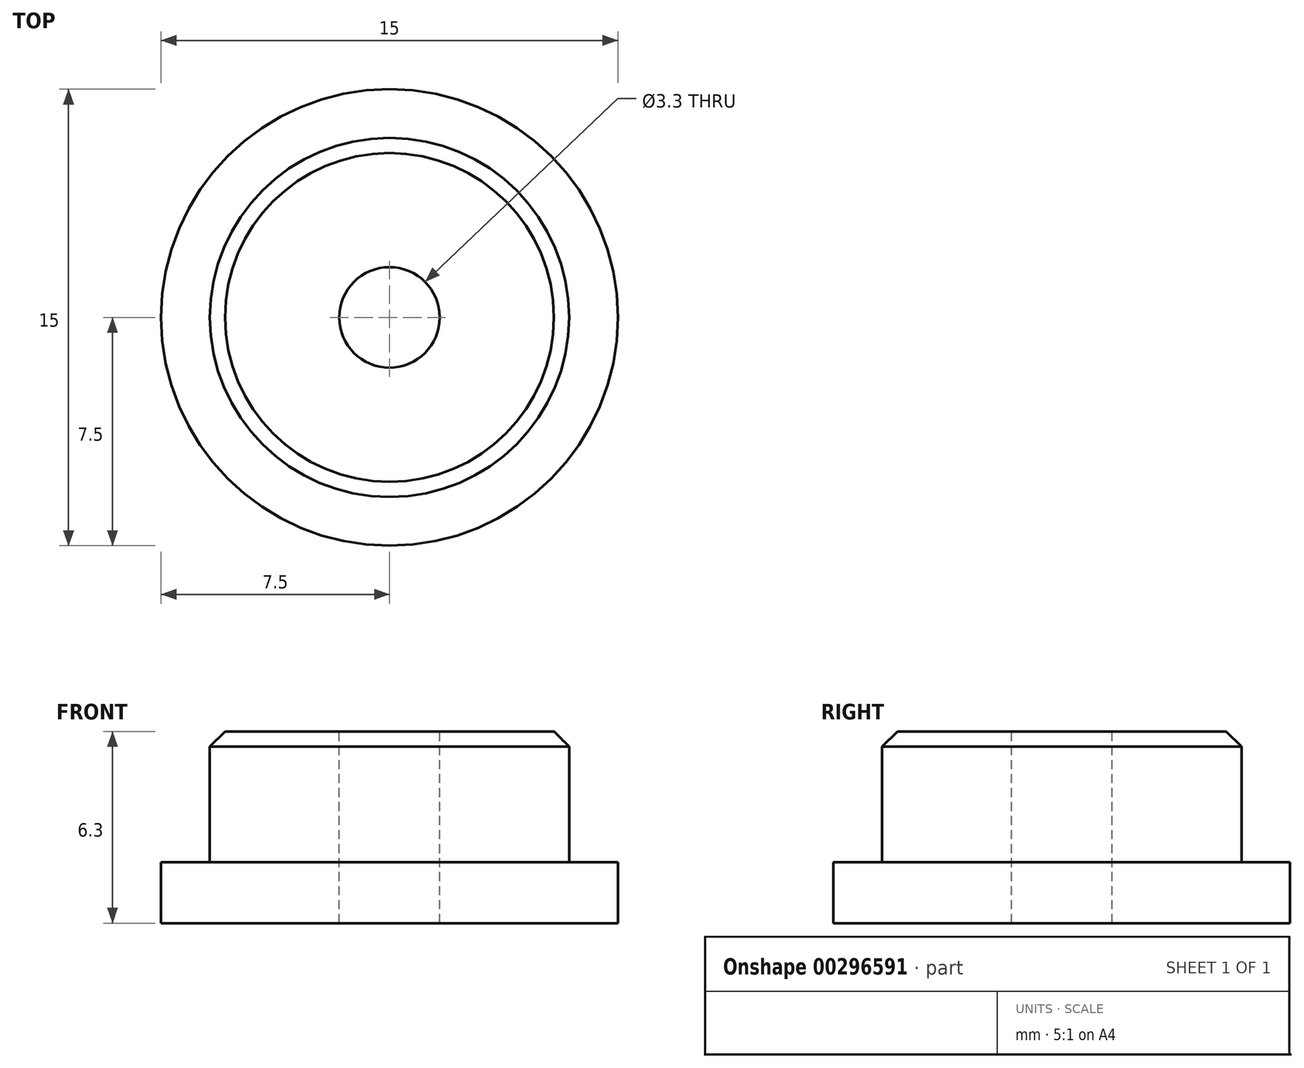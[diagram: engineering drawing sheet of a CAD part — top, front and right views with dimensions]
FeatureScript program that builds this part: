
annotation { "Feature Type Name" : "Feature", "Feature Type Description" : "" }
export const myFeature = defineFeature(function(context is Context, id is Id, definition is map)
    precondition{}
    {
        {
            var Q0;
            Q0=qCreatedBy(makeId("Top.planeOp"),FACE);
            var sketch = newSketch(context, id + "F0", { "sketchPlane" : qUnion([Q0])});
            skCircle(sketch, "E0", {"center": v(0, 0) * mm, "radius": 7.5 * mm});
            skSolve(sketch);
        }
        {
            var Q0;
            Q0 = qSketchRegion(id + "F0", true);
            extrude(context, id + "F1", {"entities" : qUnion([Q0]), "depth" : 2 * mm});
        }
        {
            var Q0;
            Q0=makeQuery(id+"F1.opExtrude","CAP_FACE",FACE,{"disambiguationData":[OSD([sQuery(id+"F0.wireOp",EDGE,"E0")])],"isStart":false});
            var sketch = newSketch(context, id + "F2", { "sketchPlane" : qUnion([Q0])});
            skCircle(sketch, "E1", {"center": v(0, 0) * mm, "radius": 5.9 * mm});
            skSolve(sketch);
        }
        {
            var Q0;
            Q0 = qSketchRegion(id + "F2", true);
            extrude(context, id + "F3", {"entities" : qUnion([Q0]), "operationType" : NewBodyOperationType.ADD, "depth" : 4.3 * mm});
        }
        {
            var Q0;
            Q0=makeQuery(id+"F3.opExtrude","CAP_FACE",FACE,{"disambiguationData":[OSD([sQuery(id+"F2.wireOp",EDGE,"E1")])],"isStart":false});
            var sketch = newSketch(context, id + "F4", { "sketchPlane" : qUnion([Q0])});
            skCircle(sketch, "E2", {"center": v(0, 0) * mm, "radius": 1.65 * mm});
            skSolve(sketch);
        }
        {
            var Q0;
            Q0 = qSketchRegion(id + "F4", true);
            extrude(context, id + "F5", {"entities" : qUnion([Q0]), "operationType" : NewBodyOperationType.REMOVE, "endBound" : BoundingType.THROUGH_ALL, "oppositeDirection" : true, "depth" : 25 * mm});
        }
        {
            var Q0;
            Q0=makeQuery(id+"F3.opExtrude","CAP_EDGE",EDGE,{"disambiguationData":[OSD([sQuery(id+"F2.wireOp",EDGE,"E1")])],"isStart":false});
            chamfer(context, id + "F6", {"entities" : qUnion([Q0]), "width" : 0.5 * mm, "tangentPropagation" : true});
        }
    });
